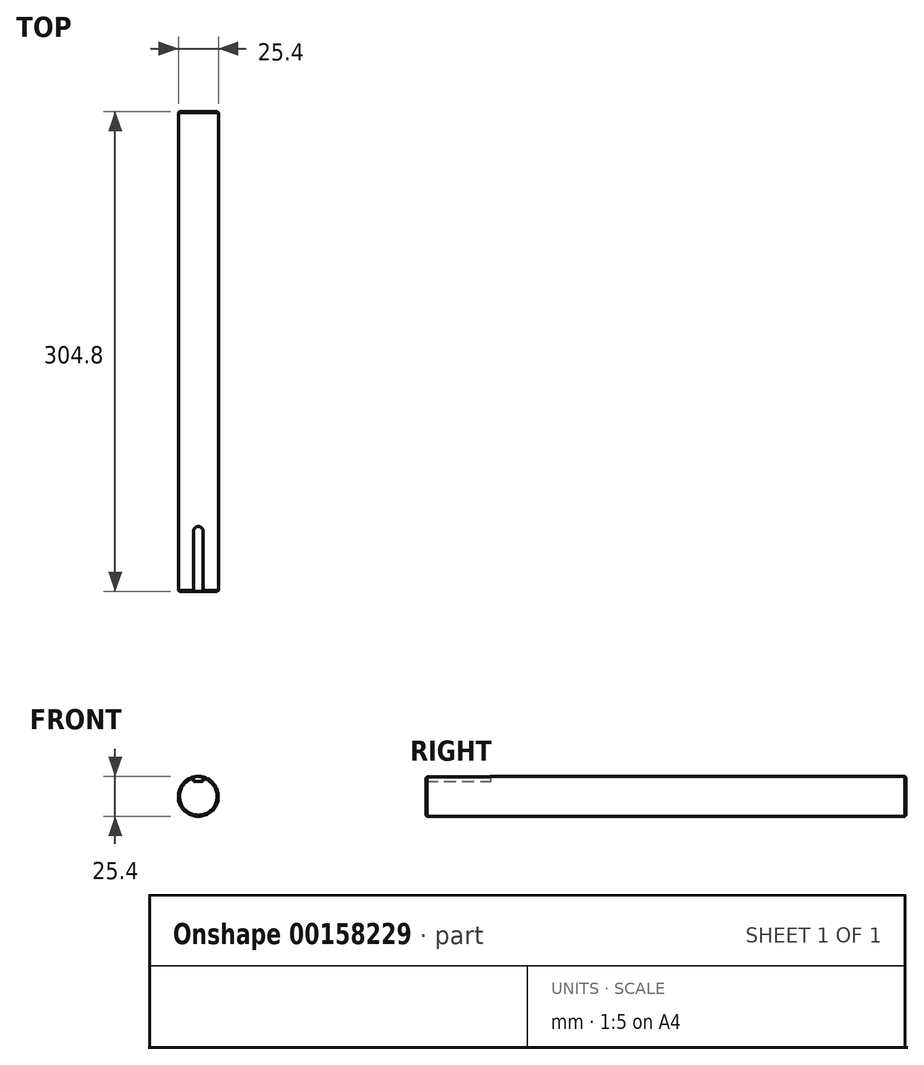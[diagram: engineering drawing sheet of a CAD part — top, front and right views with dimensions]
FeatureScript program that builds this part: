
annotation { "Feature Type Name" : "Feature", "Feature Type Description" : "" }
export const myFeature = defineFeature(function(context is Context, id is Id, definition is map)
    precondition{}
    {
        {
            var Q0;
            Q0=qCreatedBy(makeId("Front.planeOp"),FACE);
            var sketch = newSketch(context, id + "F0", { "sketchPlane" : qUnion([Q0])});
            skCircle(sketch, "E0", {"center": v(0, 0) * mm, "radius": 12.7 * mm});
            skSolve(sketch);
        }
        {
            var Q0;
            Q0 = qSketchRegion(id + "F0", true);
            extrude(context, id + "F1", {"entities" : qUnion([Q0]), "endBound" : BoundingType.SYMMETRIC, "depth" : 304.8 * mm});
        }
        {
            var Q0;
            Q0=qCreatedBy(makeId("Top.planeOp"),FACE);
            cPlane(context, id + "F2", {"entities" : qUnion([Q0]), "cplaneType" : CPlaneType.OFFSET, "offset" : 12.7 * mm, "width" : 152.4 * mm, "height" : 152.4 * mm});
        }
        {
            var Q0;
            Q0=qCreatedBy(id+"F2.planeOp",FACE);
            var sketch = newSketch(context, id + "F3", { "sketchPlane" : qUnion([Q0])});
            skLineSegment(sketch, "E1", {"start": v(0, 0) * mm, "end": v(0, -161.5) * mm, "construction": true});
            skArc(sketch, "E2", {"start": v(3.18, -114.3) * mm, "mid": v(0, -111.13) * mm, "end": v(-3.17, -114.3) * mm});
            skLineSegment(sketch, "E3.bottom", {"start": v(3.18, -156.78) * mm, "end": v(-3.17, -156.78) * mm});
            skLineSegment(sketch, "E3.left", {"start": v(3.18, -156.78) * mm, "end": v(3.17, -114.3) * mm});
            skLineSegment(sketch, "E3.right", {"start": v(-3.17, -156.78) * mm, "end": v(-3.18, -114.3) * mm});
            skPoint(sketch, "E4.orphan", {"position": v(3.17, -71.82) * mm});
            skPoint(sketch, "E5.orphan", {"position": v(-3.18, -71.82) * mm});
            skSolve(sketch);
        }
        {
            var Q0;
            Q0=makeQuery(id+"F3.imprint","IMPRINT",FACE,{"disambiguationData":[TD([[makeQuery(id+"F3.imprint","IMPRINT",EDGE,{"derivedFrom":sQuery(id+"F3.wireOp",EDGE,"E2")}),1.0]])]});
            extrude(context, id + "F4", {"entities" : qUnion([Q0]), "operationType" : NewBodyOperationType.REMOVE, "oppositeDirection" : true, "depth" : 3.17 * mm});
        }
        {
            var Q0;
            Q0=makeQuery(id+"F1.opExtrude","CAP_EDGE",EDGE,{"disambiguationData":[OSD([sQuery(id+"F0.wireOp",EDGE,"E0")])],"isStart":false});
            chamfer(context, id + "F5", {"entities" : qUnion([Q0]), "width" : 0.76 * mm, "tangentPropagation" : true});
        }
        {
            var Q0;
            Q0=makeQuery(id+"F1.opExtrude","CAP_EDGE",EDGE,{"disambiguationData":[OSD([sQuery(id+"F0.wireOp",EDGE,"E0")])],"isStart":true});
            chamfer(context, id + "F6", {"entities" : qUnion([Q0]), "width" : 0.76 * mm, "tangentPropagation" : true});
        }
    });
